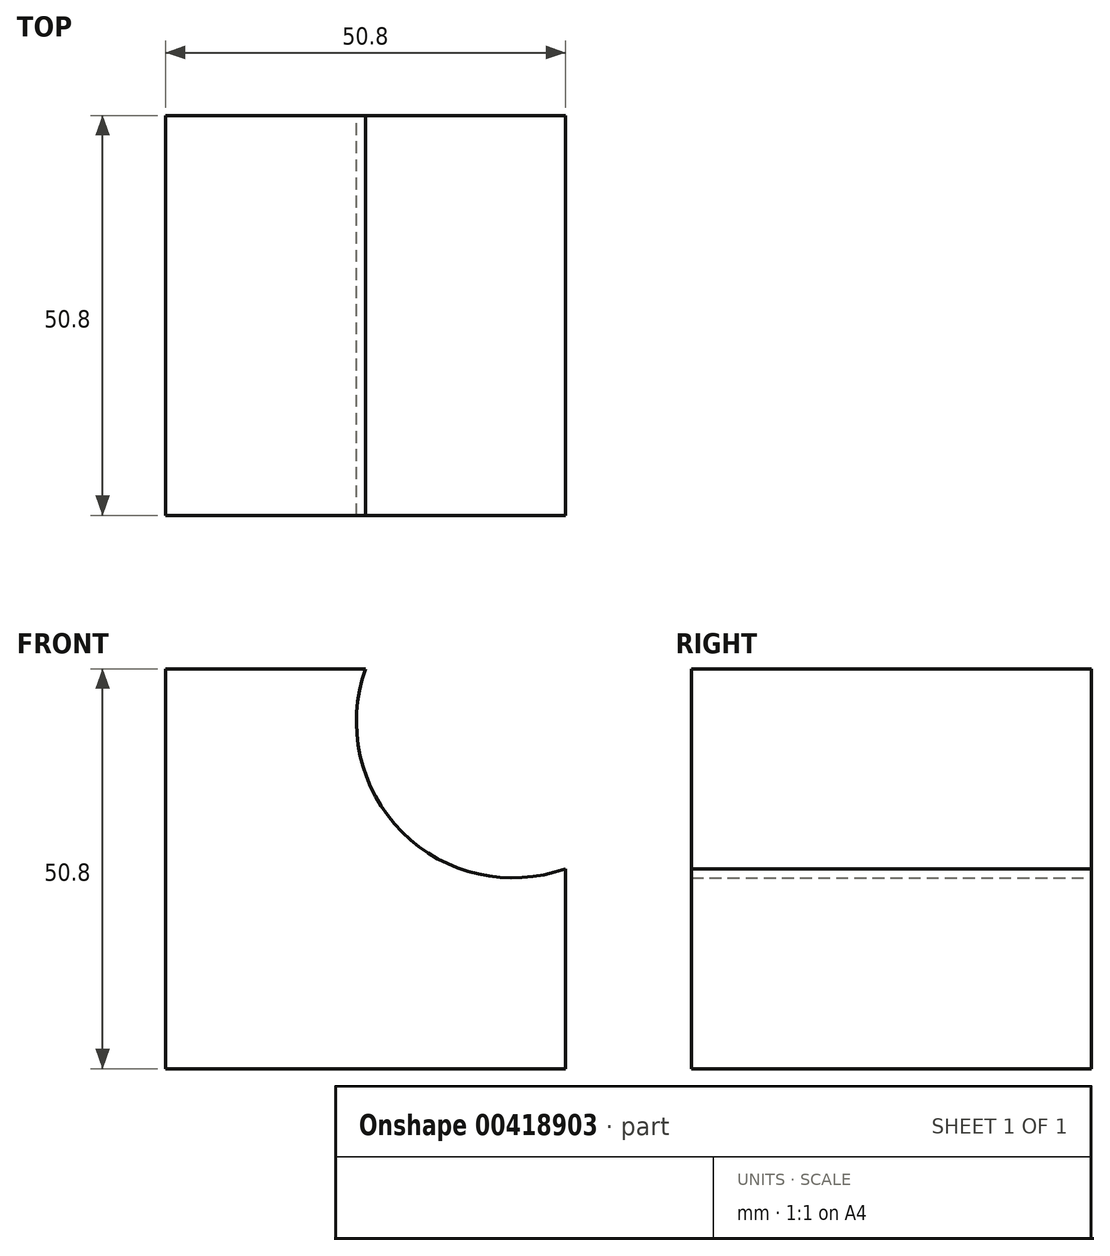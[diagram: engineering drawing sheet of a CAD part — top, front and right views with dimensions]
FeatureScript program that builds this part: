
annotation { "Feature Type Name" : "Feature", "Feature Type Description" : "" }
export const myFeature = defineFeature(function(context is Context, id is Id, definition is map)
    precondition{}
    {
        {
            var Q0;
            Q0=qCreatedBy(makeId("Front.planeOp"),FACE);
            var sketch = newSketch(context, id + "F0", { "sketchPlane" : qUnion([Q0])});
            skLineSegment(sketch, "E0", {"start": v(0, 0) * mm, "end": v(50.8, 0) * mm});
            skLineSegment(sketch, "E1", {"start": v(50.8, 0) * mm, "end": v(50.8, 25.4) * mm});
            skLineSegment(sketch, "E2", {"start": v(0, 0) * mm, "end": v(0, 50.8) * mm});
            skLineSegment(sketch, "E3", {"start": v(0, 50.8) * mm, "end": v(25.4, 50.8) * mm});
            skArc(sketch, "E4", {"start": v(25.4, 50.8) * mm, "mid": v(30.05, 30.05) * mm, "end": v(50.8, 25.4) * mm});
            skSolve(sketch);
        }
        {
            var Q0;
            Q0 = qSketchRegion(id + "F0", true);
            extrude(context, id + "F1", {"entities" : qUnion([Q0]), "depth" : 50.8 * mm});
        }
    });
